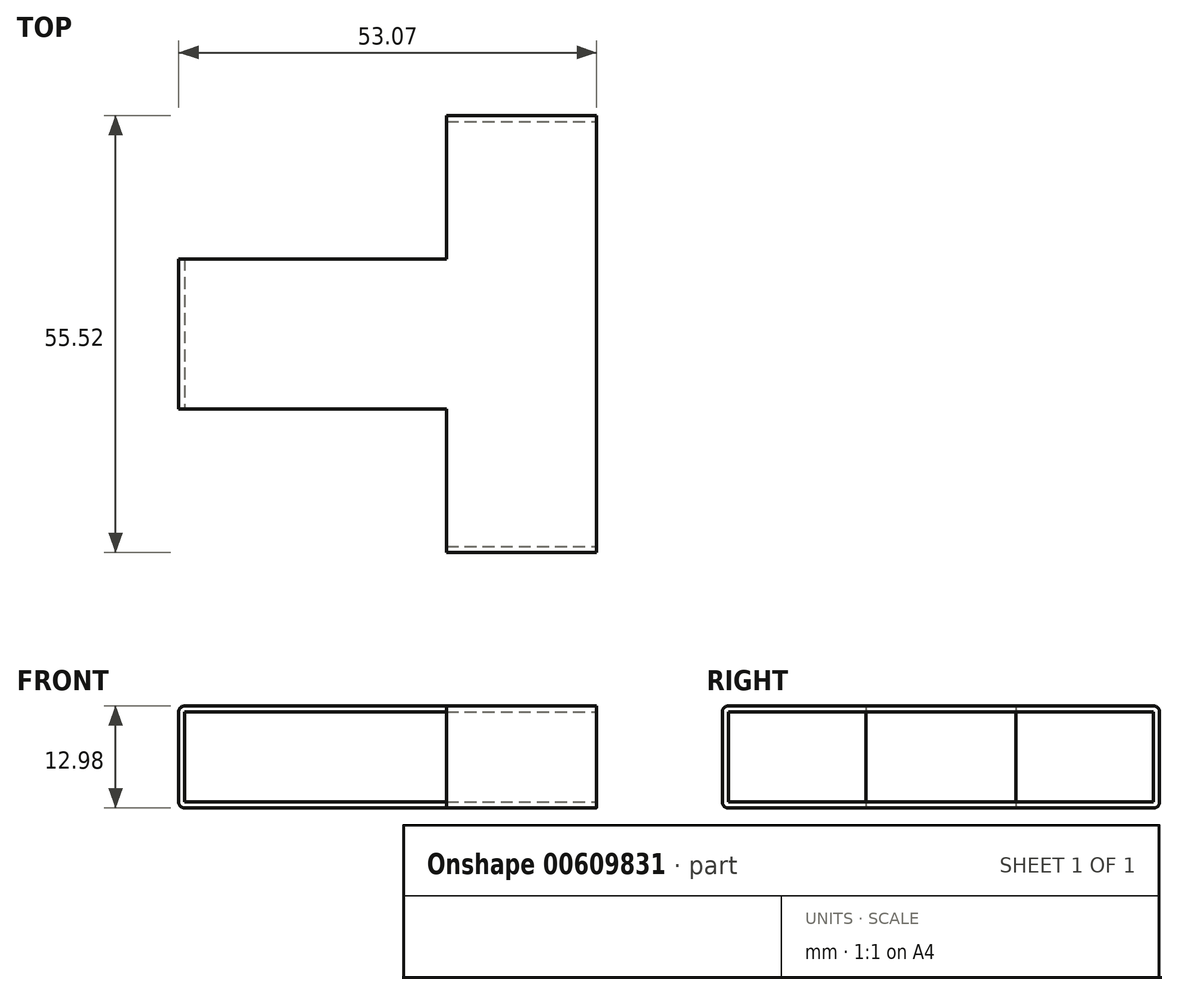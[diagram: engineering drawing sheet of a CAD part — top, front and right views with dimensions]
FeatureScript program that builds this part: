
annotation { "Feature Type Name" : "Feature", "Feature Type Description" : "" }
export const myFeature = defineFeature(function(context is Context, id is Id, definition is map)
    precondition{}
    {
        {
            var Q0;
            Q0=qCreatedBy(makeId("Top.planeOp"),FACE);
            var sketch = newSketch(context, id + "F0", { "sketchPlane" : qUnion([Q0])});
            skLineSegment(sketch, "E0.bottom", {"start": v(-42.78, 27) * mm, "end": v(42.78, 27) * mm, "construction": true});
            skLineSegment(sketch, "E0.top", {"start": v(-42.78, -27) * mm, "end": v(42.78, -27) * mm, "construction": true});
            skLineSegment(sketch, "E0.left", {"start": v(-42.78, 27) * mm, "end": v(-42.78, -27) * mm, "construction": true});
            skLineSegment(sketch, "E0.right", {"start": v(42.78, 27) * mm, "end": v(42.78, -27) * mm, "construction": true});
            skPoint(sketch, "E0.middle", {"position": v(0, 0) * mm});
            skLineSegment(sketch, "E1", {"start": v(0, 27) * mm, "end": v(0, -27) * mm, "construction": true});
            skLineSegment(sketch, "E2", {"start": v(0, 0) * mm, "end": v(-42.78, 0) * mm, "construction": true});
            skLineSegment(sketch, "E3.0", {"start": v(9.52, 27.76) * mm, "end": v(9.52, -27.76) * mm});
            skLineSegment(sketch, "E4.0", {"start": v(-9.53, 9.53) * mm, "end": v(-43.54, 9.53) * mm});
            skLineSegment(sketch, "E5.0", {"start": v(-9.53, -9.53) * mm, "end": v(-43.54, -9.53) * mm});
            skLineSegment(sketch, "E6", {"start": v(-9.53, 27.76) * mm, "end": v(9.52, 27.76) * mm});
            skLineSegment(sketch, "E7", {"start": v(9.53, -27.76) * mm, "end": v(-9.52, -27.76) * mm});
            skLineSegment(sketch, "E8", {"start": v(-43.54, 9.52) * mm, "end": v(-43.54, -9.53) * mm});
            skLineSegment(sketch, "E9.trimOffspring", {"start": v(-9.53, -9.53) * mm, "end": v(-9.53, -27.76) * mm});
            skLineSegment(sketch, "E10", {"start": v(-9.53, 9.53) * mm, "end": v(-9.53, 27.76) * mm});
            skSolve(sketch);
        }
        {
            var Q0;
            Q0 = qSketchRegion(id + "F0", true);
            extrude(context, id + "F1", {"entities" : qUnion([Q0]), "depth" : 6.5 * mm, "offsetDistance" : 25.4 * mm, "hasSecondDirection" : true, "secondDirectionOppositeDirection" : true, "secondDirectionDepth" : 6.5 * mm});
        }
        {
            var Q0;
            Q0=qCreatedBy(makeId("Top.planeOp"),FACE);
            var sketch = newSketch(context, id + "F2", { "sketchPlane" : qUnion([Q0])});
            skLineSegment(sketch, "E11.0", {"start": v(-42.78, 27) * mm, "end": v(42.78, 27) * mm});
            skLineSegment(sketch, "E11.1", {"start": v(42.78, 27) * mm, "end": v(42.78, -27) * mm});
            skLineSegment(sketch, "E11.2", {"start": v(-42.78, -27) * mm, "end": v(42.78, -27) * mm});
            skLineSegment(sketch, "E11.3", {"start": v(-42.78, 27) * mm, "end": v(-42.78, -27) * mm});
            skSolve(sketch);
        }
        {
            var Q0;
            Q0 = qSketchRegion(id + "F2", true);
            extrude(context, id + "F3", {"entities" : qUnion([Q0]), "operationType" : NewBodyOperationType.REMOVE, "oppositeDirection" : true, "depth" : 5.73 * mm, "offsetDistance" : 25.4 * mm, "hasSecondDirection" : true, "secondDirectionOppositeDirection" : false, "secondDirectionDepth" : 5.73 * mm});
        }
        {
            var Q0;
            Q0=makeQuery(id+"F1.opExtrude","CAP_EDGE",EDGE,{"disambiguationData":[OSD([sQuery(id+"F0.wireOp",EDGE,"E7")])],"isStart":false});
            var Q1;
            Q1=makeQuery(id+"F1.opExtrude","CAP_EDGE",EDGE,{"disambiguationData":[OSD([sQuery(id+"F0.wireOp",EDGE,"E7")])],"isStart":true});
            var Q2;
            Q2=makeQuery(id+"F1.opExtrude","CAP_EDGE",EDGE,{"disambiguationData":[OSD([sQuery(id+"F0.wireOp",EDGE,"E6")])],"isStart":false});
            var Q3;
            Q3=makeQuery(id+"F1.opExtrude","CAP_EDGE",EDGE,{"disambiguationData":[OSD([sQuery(id+"F0.wireOp",EDGE,"E6")])],"isStart":true});
            var Q4;
            Q4=makeQuery(id+"F1.opExtrude","CAP_EDGE",EDGE,{"disambiguationData":[OSD([sQuery(id+"F0.wireOp",EDGE,"E8")])],"isStart":true});
            var Q5;
            Q5=makeQuery(id+"F1.opExtrude","CAP_EDGE",EDGE,{"disambiguationData":[OSD([sQuery(id+"F0.wireOp",EDGE,"E8")])],"isStart":false});
            fillet(context, id + "F4", {"entities" : qUnion([Q0, Q1, Q2, Q3, Q4, Q5]), "radius" : 0.76 * mm, "tangentPropagation" : true, "allowEdgeOverflow" : false});
        }
    });
